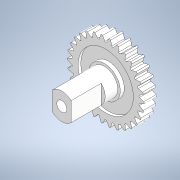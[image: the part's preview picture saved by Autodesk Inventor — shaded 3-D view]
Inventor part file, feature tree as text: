
AUTODESK INVENTOR PART (.ipt)
format: ipt  version: 2022.3 (Build 263350000, 350)  size: 257,024 bytes
history: native  units: mm
features: extrude x2, sketch x2, projected_geometry x2, imported_body x1
ambient origin geometry x8: Origin, YZ Plane, XZ Plane, XY Plane, X Axis, Y Axis, Z Axis, Center Point
bodies: Solid1 (feature_tree)
feature tree (7):
  extrude  "Extrusion1"  Depth=10.0mm TaperAngle=0.0deg
  extrude  "Extrusion2"  [1 undecoded]
  sketch  "Sketch1"  dims[d0=10.0mm d1=0.0mm d2=2.0mm d3=0.0mm]
  projected_geometry  "Projected Loop1"
  sketch  "Sketch2"
  projected_geometry  "Projected Loop2"
  imported_body  "Base1"
note: 1 required parameter value undecoded (feature->parameter linkage not recoverable at this tier; creation-order binding heuristic only, values carry confidence <= 0.55)
